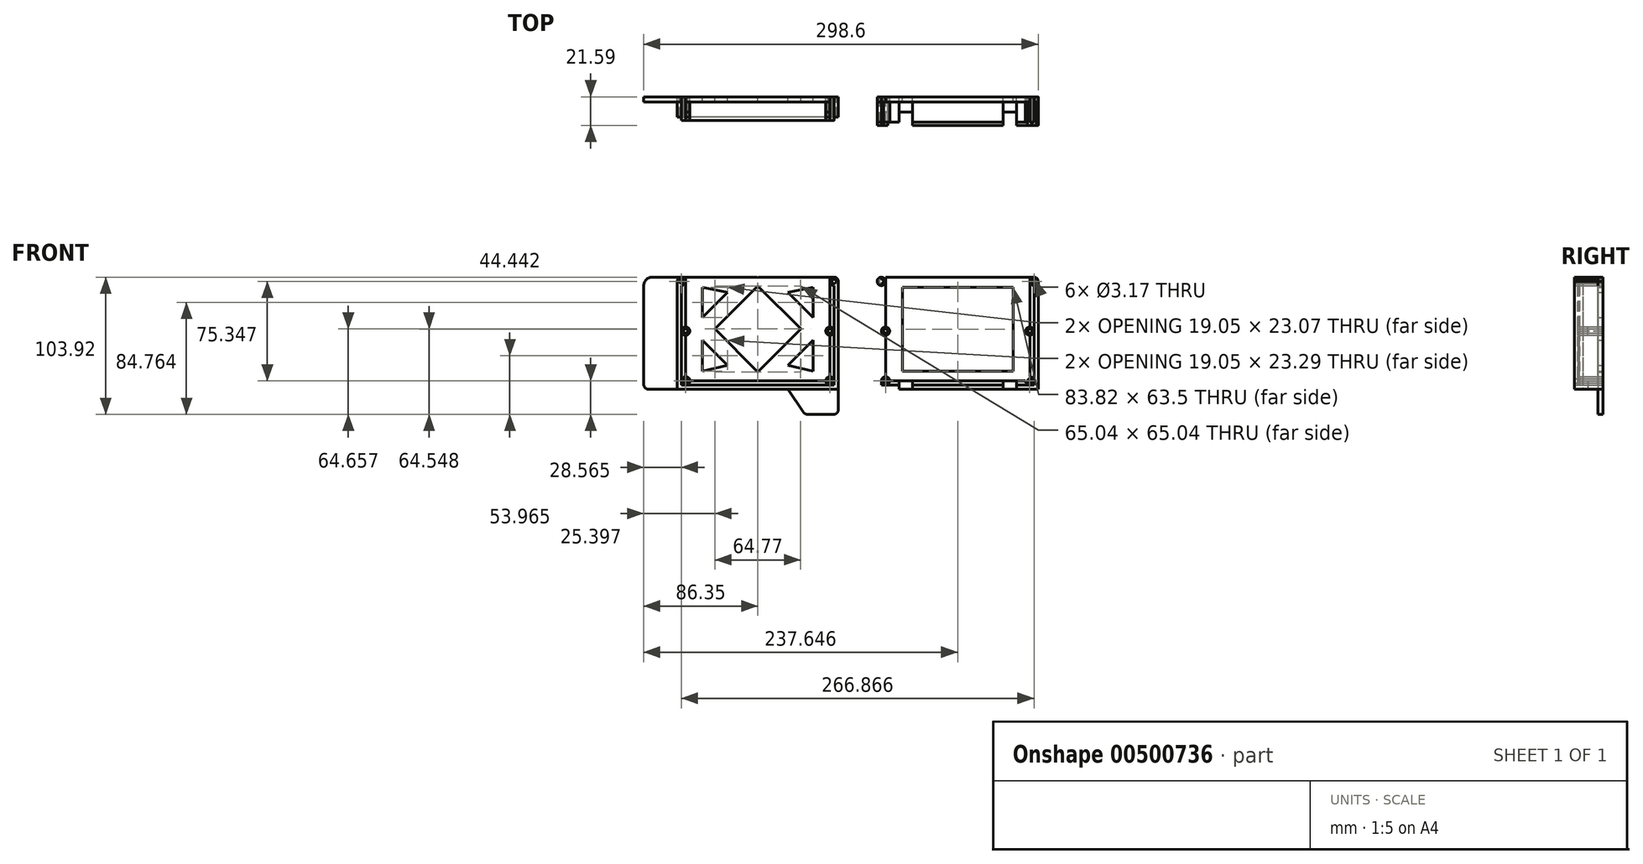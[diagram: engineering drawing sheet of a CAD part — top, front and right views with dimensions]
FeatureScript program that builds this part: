
annotation { "Feature Type Name" : "Feature", "Feature Type Description" : "" }
export const myFeature = defineFeature(function(context is Context, id is Id, definition is map)
    precondition{}
    {
        {
            var Q0;
            Q0=qCreatedBy(makeId("Front.planeOp"),FACE);
            var sketch = newSketch(context, id + "F0", { "sketchPlane" : qUnion([Q0])});
            skLineSegment(sketch, "E0.bottom", {"start": v(57.79, -40.85) * mm, "end": v(-57.78, -40.85) * mm});
            skLineSegment(sketch, "E0.top", {"start": v(57.79, 40.85) * mm, "end": v(-57.79, 40.85) * mm});
            skPoint(sketch, "E0.middle", {"position": v(0, 0) * mm});
            skLineSegment(sketch, "E1.0", {"start": v(51.44, -37.67) * mm, "end": v(-51.34, -37.67) * mm});
            skLineSegment(sketch, "E2.0", {"start": v(-54.61, -34.5) * mm, "end": v(-54.61, -3.17) * mm});
            skLineSegment(sketch, "E3.0", {"start": v(54.6, -34.5) * mm, "end": v(54.6, -3.17) * mm});
            skLineSegment(sketch, "E4.0", {"start": v(-41.91, -30.27) * mm, "end": v(-41.91, -6.98) * mm});
            skLineSegment(sketch, "E5.0", {"start": v(41.91, -30.27) * mm, "end": v(41.91, -6.98) * mm});
            skLineSegment(sketch, "E6", {"start": v(-41.91, 10.16) * mm, "end": v(-22.86, 29.21) * mm});
            skLineSegment(sketch, "E7", {"start": v(-41.91, -6.98) * mm, "end": v(-22.86, -26.03) * mm});
            skLineSegment(sketch, "E8", {"start": v(22.86, -26.03) * mm, "end": v(41.9, -6.98) * mm});
            skLineSegment(sketch, "E9", {"start": v(41.9, 10.16) * mm, "end": v(22.86, 29.21) * mm});
            skLineSegment(sketch, "E10.trimOffspring", {"start": v(-41.91, 10.16) * mm, "end": v(-41.91, 33.23) * mm});
            skLineSegment(sketch, "E11.trimOffspring", {"start": v(41.91, 10.16) * mm, "end": v(41.91, 33.23) * mm});
            skLineSegment(sketch, "E12.trimOffspring", {"start": v(-22.86, 29.21) * mm, "end": v(-41.91, 33.23) * mm});
            skLineSegment(sketch, "E13.trimOffspring", {"start": v(-22.86, -26.03) * mm, "end": v(-41.91, -30.27) * mm});
            skLineSegment(sketch, "E14.trimOffspring", {"start": v(41.91, 33.23) * mm, "end": v(22.86, 29.21) * mm});
            skLineSegment(sketch, "E15.trimOffspring", {"start": v(41.91, -30.27) * mm, "end": v(22.86, -26.03) * mm});
            skLineSegment(sketch, "E16.0", {"start": v(-32.52, 1.59) * mm, "end": v(0, 34.1) * mm});
            skLineSegment(sketch, "E17.0", {"start": v(32.52, 1.59) * mm, "end": v(0, 34.1) * mm});
            skLineSegment(sketch, "E18.0", {"start": v(0, -30.93) * mm, "end": v(32.52, 1.59) * mm});
            skLineSegment(sketch, "E19.0", {"start": v(-32.52, 1.59) * mm, "end": v(0, -30.93) * mm});
            skArc(sketch, "E20", {"start": v(-54.61, -3.17) * mm, "mid": v(-51.44, 0) * mm, "end": v(-54.61, 3.18) * mm});
            skPoint(sketch, "E20.centerSnap0", {"position": v(-57.79, 0) * mm});
            skPoint(sketch, "E21.centerSnap0", {"position": v(57.79, 0) * mm});
            skArc(sketch, "E22", {"start": v(54.6, -34.5) * mm, "mid": v(52.36, -35.43) * mm, "end": v(51.44, -37.67) * mm});
            skPoint(sketch, "E23.second.point", {"position": v(54.6, 38.74) * mm});
            skPoint(sketch, "E23.third.point", {"position": v(60.92, 37.5) * mm});
            skLineSegment(sketch, "E24.trimOffspring", {"start": v(54.6, 3.18) * mm, "end": v(54.6, 40.85) * mm});
            skLineSegment(sketch, "E25.trimOffspring", {"start": v(-54.61, 3.18) * mm, "end": v(-54.61, 40.85) * mm});
            skLineSegment(sketch, "E26", {"start": v(-60.95, 37.67) * mm, "end": v(-60.95, -44.02) * mm});
            skLineSegment(sketch, "E27.0", {"start": v(60.96, -44.02) * mm, "end": v(-60.95, -44.02) * mm});
            skLineSegment(sketch, "E28", {"start": v(-57.79, 40.85) * mm, "end": v(-57.78, -40.85) * mm});
            skLineSegment(sketch, "E29", {"start": v(57.79, 40.85) * mm, "end": v(57.79, -40.85) * mm});
            skLineSegment(sketch, "E30", {"start": v(60.92, 37.5) * mm, "end": v(60.96, -44.02) * mm});
            skPoint(sketch, "E21.center.orphan", {"position": v(54.6, 0) * mm});
            skCircle(sketch, "E31", {"center": v(54.6, 0) * mm, "radius": 3.18 * mm});
            skCircle(sketch, "E32", {"center": v(54.6, 0) * mm, "radius": 1.6 * mm});
            skCircle(sketch, "E33", {"center": v(-54.61, 0) * mm, "radius": 3.18 * mm});
            skCircle(sketch, "E34", {"center": v(-54.61, 0) * mm, "radius": 1.6 * mm});
            skCircle(sketch, "E35", {"center": v(54.6, -37.67) * mm, "radius": 1.59 * mm});
            skCircle(sketch, "E36", {"center": v(54.6, -37.67) * mm, "radius": 3.18 * mm});
            skCircle(sketch, "E37", {"center": v(-54.51, -37.67) * mm, "radius": 3.17 * mm});
            skCircle(sketch, "E38", {"center": v(-54.51, -37.67) * mm, "radius": 1.59 * mm});
            skCircle(sketch, "E39", {"center": v(-57.79, 37.67) * mm, "radius": 3.16 * mm});
            skCircle(sketch, "E40", {"center": v(57.79, 37.67) * mm, "radius": 3.18 * mm});
            skCircle(sketch, "E41", {"center": v(-57.79, 37.67) * mm, "radius": 1.59 * mm});
            skCircle(sketch, "E42", {"center": v(57.79, 37.67) * mm, "radius": 1.6 * mm});
            skLineSegment(sketch, "E43", {"start": v(75.65, 45.82) * mm, "end": v(75.65, -59.82) * mm, "construction": true});
            skCircle(sketch, "E44.MirrorC", {"center": v(93.51, 37.67) * mm, "radius": 1.6 * mm});
            skCircle(sketch, "E45.MirrorC", {"center": v(209.08, 37.67) * mm, "radius": 1.59 * mm});
            skCircle(sketch, "E46.MirrorC", {"center": v(205.8, -37.67) * mm, "radius": 1.59 * mm});
            skCircle(sketch, "E47.MirrorC", {"center": v(96.69, 0) * mm, "radius": 1.6 * mm});
            skCircle(sketch, "E48.MirrorC", {"center": v(205.9, 0) * mm, "radius": 3.18 * mm});
            skCircle(sketch, "E49.MirrorC", {"center": v(96.69, -37.67) * mm, "radius": 1.59 * mm});
            skArc(sketch, "E50.MirrorCS", {"start": v(205.9, -3.17) * mm, "mid": v(202.73, 0) * mm, "end": v(205.9, 3.18) * mm});
            skCircle(sketch, "E51.MirrorC", {"center": v(96.69, 0) * mm, "radius": 3.18 * mm});
            skLineSegment(sketch, "E52.MirrorCS", {"start": v(99.86, -37.67) * mm, "end": v(202.63, -37.67) * mm});
            skLineSegment(sketch, "E53.MirrorCS", {"start": v(209.08, 40.85) * mm, "end": v(209.08, -40.85) * mm});
            skCircle(sketch, "E54.MirrorC", {"center": v(205.9, 0) * mm, "radius": 1.6 * mm});
            skLineSegment(sketch, "E55.MirrorCS", {"start": v(205.9, -34.5) * mm, "end": v(205.9, -3.17) * mm});
            skLineSegment(sketch, "E56.MirrorCS", {"start": v(96.69, -34.5) * mm, "end": v(96.69, -3.17) * mm});
            skPoint(sketch, "E57.MirrorP", {"position": v(209.08, 0) * mm});
            skLineSegment(sketch, "E58.MirrorCS", {"start": v(212.25, 37.67) * mm, "end": v(212.25, -44.02) * mm});
            skArc(sketch, "E59.MirrorCS", {"start": v(96.69, -34.5) * mm, "mid": v(98.93, -35.43) * mm, "end": v(99.86, -37.67) * mm});
            skCircle(sketch, "E60.MirrorC", {"center": v(209.08, 37.67) * mm, "radius": 3.16 * mm});
            skCircle(sketch, "E61.MirrorC", {"center": v(93.51, 37.67) * mm, "radius": 3.18 * mm});
            skLineSegment(sketch, "E62.MirrorCS", {"start": v(96.69, 3.18) * mm, "end": v(96.69, 40.85) * mm});
            skLineSegment(sketch, "E63.MirrorCS", {"start": v(93.51, 40.85) * mm, "end": v(209.08, 40.85) * mm});
            skPoint(sketch, "E64.MirrorP", {"position": v(90.38, 37.5) * mm});
            skLineSegment(sketch, "E65.MirrorCS", {"start": v(93.51, -40.85) * mm, "end": v(209.08, -40.85) * mm});
            skLineSegment(sketch, "E66.MirrorCS", {"start": v(90.38, 37.5) * mm, "end": v(90.34, -44.02) * mm});
            skCircle(sketch, "E67.MirrorC", {"center": v(205.8, -37.67) * mm, "radius": 3.17 * mm});
            skCircle(sketch, "E68.MirrorC", {"center": v(96.69, -37.67) * mm, "radius": 3.18 * mm});
            skLineSegment(sketch, "E69.MirrorCS", {"start": v(90.34, -44.02) * mm, "end": v(212.25, -44.02) * mm});
            skPoint(sketch, "E70.MirrorP", {"position": v(151.3, 0) * mm});
            skPoint(sketch, "E71.MirrorP", {"position": v(93.51, 0) * mm});
            skPoint(sketch, "E72.MirrorP", {"position": v(96.69, 38.74) * mm});
            skLineSegment(sketch, "E73.MirrorCS", {"start": v(205.9, 3.18) * mm, "end": v(205.9, 40.85) * mm});
            skLineSegment(sketch, "E74.MirrorCS", {"start": v(93.51, 40.85) * mm, "end": v(93.51, -40.85) * mm});
            skLineSegment(sketch, "E75", {"start": v(109.39, 33.23) * mm, "end": v(193.2, 33.23) * mm});
            skLineSegment(sketch, "E76", {"start": v(109.39, 33.23) * mm, "end": v(109.39, -30.27) * mm});
            skLineSegment(sketch, "E77", {"start": v(109.39, -30.27) * mm, "end": v(193.2, -30.27) * mm});
            skLineSegment(sketch, "E78", {"start": v(193.2, 33.23) * mm, "end": v(193.2, -30.27) * mm});
            skLineSegment(sketch, "E79.0", {"start": v(185.59, -44.02) * mm, "end": v(185.59, -37.67) * mm});
            skLineSegment(sketch, "E80", {"start": v(195.75, -37.67) * mm, "end": v(195.75, -44.02) * mm});
            skLineSegment(sketch, "E81", {"start": v(117, -37.67) * mm, "end": v(117, -44.02) * mm});
            skLineSegment(sketch, "E82", {"start": v(106.85, -37.67) * mm, "end": v(106.85, -44.02) * mm});
            skLineSegment(sketch, "E83.0", {"start": v(-86.35, 34.5) * mm, "end": v(-86.35, -40.21) * mm});
            skLineSegment(sketch, "E84", {"start": v(-57.79, 40.85) * mm, "end": v(-80, 40.85) * mm});
            skLineSegment(sketch, "E85", {"start": v(-60.95, -44.02) * mm, "end": v(-82.54, -44.02) * mm});
            skPoint(sketch, "E86.visualSharp", {"position": v(-86.35, 40.85) * mm});
            skArc(sketch, "E86.filletArc", {"start": v(-80, 40.85) * mm, "mid": v(-84.49, 38.99) * mm, "end": v(-86.35, 34.5) * mm});
            skPoint(sketch, "E87.visualSharp", {"position": v(-86.35, -44.02) * mm});
            skArc(sketch, "E87.filletArc", {"start": v(-86.35, -40.21) * mm, "mid": v(-85.23, -42.9) * mm, "end": v(-82.54, -44.02) * mm});
            skLineSegment(sketch, "E88.0", {"start": v(57.15, -63.07) * mm, "end": v(37.6, -63.07) * mm});
            skLineSegment(sketch, "E89", {"start": v(60.96, -44.02) * mm, "end": v(60.96, -59.26) * mm});
            skLineSegment(sketch, "E90", {"start": v(22.86, -44.02) * mm, "end": v(34.43, -61.38) * mm});
            skPoint(sketch, "E91.visualSharp", {"position": v(60.96, -63.07) * mm});
            skArc(sketch, "E91.filletArc", {"start": v(57.15, -63.07) * mm, "mid": v(59.84, -61.96) * mm, "end": v(60.96, -59.26) * mm});
            skPoint(sketch, "E92.visualSharp", {"position": v(35.56, -63.07) * mm});
            skArc(sketch, "E92.filletArc", {"start": v(34.43, -61.38) * mm, "mid": v(35.8, -62.62) * mm, "end": v(37.6, -63.07) * mm});
            skSolve(sketch);
        }
        {
            var Q0;
            {var subQ18=sQuery(id+"F0.wireOp",EDGE,"E55.MirrorCS");Q0=makeQuery(id+"F0.imprint","IMPRINT",FACE,{"disambiguationData":[TD([[makeQuery(id+"F0.imprint","IMPRINT",EDGE,{"derivedFrom":subQ18}),1.0]])]});}
            var Q1;
            {var subQ0=sQuery(id+"F0.wireOp",EDGE,"E74.MirrorCS");var subQ1=sQuery(id+"F0.wireOp",EDGE,"E44.MirrorC");var subQ2=makeQuery(id+"F0.imprint","INTERSECT",VERTEX,{"disambiguationData":[OD(0.0)],"derivedFrom":[subQ1,subQ0]});Q1=makeQuery(id+"F0.imprint","IMPRINT",FACE,{"disambiguationData":[TD([[makeQuery(id+"F0.imprint","IMPRINT",EDGE,{"disambiguationData":[TD([[subQ2,1.0]])],"derivedFrom":subQ1}),-1.0]])]});}
            var Q2;
            {var subQ0=sQuery(id+"F0.wireOp",EDGE,"E74.MirrorCS");var subQ1=sQuery(id+"F0.wireOp",EDGE,"E44.MirrorC");var subQ2=makeQuery(id+"F0.imprint","INTERSECT",VERTEX,{"disambiguationData":[OD(0.0)],"derivedFrom":[subQ1,subQ0]});Q2=makeQuery(id+"F0.imprint","IMPRINT",FACE,{"disambiguationData":[TD([[makeQuery(id+"F0.imprint","IMPRINT",EDGE,{"disambiguationData":[TD([[subQ2,-1.0]])],"derivedFrom":subQ1}),-1.0]])]});}
            var Q3;
            Q3=makeQuery(id+"F0.imprint","IMPRINT",FACE,{"disambiguationData":[TD([[makeQuery(id+"F0.imprint","IMPRINT",EDGE,{"derivedFrom":sQuery(id+"F0.wireOp",EDGE,"E49.MirrorC")}),-1.0]])]});
            var Q4;
            Q4=makeQuery(id+"F0.imprint","IMPRINT",FACE,{"disambiguationData":[TD([[makeQuery(id+"F0.imprint","IMPRINT",EDGE,{"derivedFrom":sQuery(id+"F0.wireOp",EDGE,"E46.MirrorC")}),-1.0]])]});
            var Q5;
            {var subQ0=sQuery(id+"F0.wireOp",EDGE,"E53.MirrorCS");var subQ1=sQuery(id+"F0.wireOp",EDGE,"E45.MirrorC");var subQ2=makeQuery(id+"F0.imprint","INTERSECT",VERTEX,{"disambiguationData":[OD(0.0)],"derivedFrom":[subQ1,subQ0]});Q5=makeQuery(id+"F0.imprint","IMPRINT",FACE,{"disambiguationData":[TD([[makeQuery(id+"F0.imprint","IMPRINT",EDGE,{"disambiguationData":[TD([[subQ2,1.0]])],"derivedFrom":subQ1}),-1.0]])]});}
            var Q6;
            {var subQ0=sQuery(id+"F0.wireOp",EDGE,"E53.MirrorCS");var subQ1=sQuery(id+"F0.wireOp",EDGE,"E45.MirrorC");var subQ2=makeQuery(id+"F0.imprint","INTERSECT",VERTEX,{"disambiguationData":[OD(0.0)],"derivedFrom":[subQ1,subQ0]});Q6=makeQuery(id+"F0.imprint","IMPRINT",FACE,{"disambiguationData":[TD([[makeQuery(id+"F0.imprint","IMPRINT",EDGE,{"disambiguationData":[TD([[subQ2,-1.0]])],"derivedFrom":subQ1}),-1.0]])]});}
            extrude(context, id + "F1", {"entities" : qUnion([Q0, Q1, Q2, Q3, Q4, Q5, Q6]), "depth" : 3.8 * mm});
        }
        {
            var Q0;
            Q0=makeQuery(id+"F0.imprint","IMPRINT",FACE,{"disambiguationData":[TD([[makeQuery(id+"F0.imprint","IMPRINT",EDGE,{"derivedFrom":sQuery(id+"F0.wireOp",EDGE,"E47.MirrorC")}),1.0]])]});
            var Q1;
            {var subQ0=sQuery(id+"F0.wireOp",EDGE,"E81");var subQ1=sQuery(id+"F0.wireOp",EDGE,"E52.MirrorCS");var subQ2=makeQuery(id+"F0.imprint","INTERSECT",VERTEX,{"derivedFrom":[subQ1,subQ0]});Q1=makeQuery(id+"F0.imprint","IMPRINT",FACE,{"disambiguationData":[TD([[makeQuery(id+"F0.imprint","IMPRINT",EDGE,{"disambiguationData":[TD([[subQ2,1.0]])],"derivedFrom":subQ1}),-1.0]])]});}
            var Q2;
            {var subQ0=sQuery(id+"F0.wireOp",EDGE,"E82");var subQ1=sQuery(id+"F0.wireOp",EDGE,"E65.MirrorCS");var subQ2=makeQuery(id+"F0.imprint","INTERSECT",VERTEX,{"derivedFrom":[subQ1,subQ0]});Q2=makeQuery(id+"F0.imprint","IMPRINT",FACE,{"disambiguationData":[TD([[makeQuery(id+"F0.imprint","IMPRINT",EDGE,{"disambiguationData":[TD([[subQ2,-1.0]])],"derivedFrom":subQ1}),-1.0]])]});}
            var Q3;
            {var subQ0=sQuery(id+"F0.wireOp",EDGE,"E79.0");var subQ1=sQuery(id+"F0.wireOp",EDGE,"E52.MirrorCS");var subQ2=makeQuery(id+"F0.imprint","INTERSECT",VERTEX,{"derivedFrom":[subQ1,subQ0]});Q3=makeQuery(id+"F0.imprint","IMPRINT",FACE,{"disambiguationData":[TD([[makeQuery(id+"F0.imprint","IMPRINT",EDGE,{"disambiguationData":[TD([[subQ2,-1.0]])],"derivedFrom":subQ1}),-1.0]])]});}
            var Q4;
            {var subQ0=sQuery(id+"F0.wireOp",EDGE,"E79.0");var subQ1=sQuery(id+"F0.wireOp",EDGE,"E65.MirrorCS");var subQ2=makeQuery(id+"F0.imprint","INTERSECT",VERTEX,{"derivedFrom":[subQ1,subQ0]});Q4=makeQuery(id+"F0.imprint","IMPRINT",FACE,{"disambiguationData":[TD([[makeQuery(id+"F0.imprint","IMPRINT",EDGE,{"disambiguationData":[TD([[subQ2,-1.0]])],"derivedFrom":subQ1}),-1.0]])]});}
            var Q5;
            Q5=makeQuery(id+"F0.imprint","IMPRINT",FACE,{"disambiguationData":[TD([[makeQuery(id+"F0.imprint","IMPRINT",EDGE,{"derivedFrom":sQuery(id+"F0.wireOp",EDGE,"E54.MirrorC")}),1.0]])]});
            extrude(context, id + "F2", {"entities" : qUnion([Q0, Q1, Q2, Q3, Q4, Q5]), "operationType" : NewBodyOperationType.ADD, "depth" : 11.43 * mm});
        }
        {
            var Q0;
            {var subQ0=sQuery(id+"F0.wireOp",EDGE,"E63.MirrorCS");var subQ1=sQuery(id+"F0.wireOp",EDGE,"E61.MirrorC");var subQ2=makeQuery(id+"F0.imprint","INTERSECT",VERTEX,{"derivedFrom":[subQ1,subQ0]});Q0=makeQuery(id+"F0.imprint","IMPRINT",FACE,{"disambiguationData":[TD([[makeQuery(id+"F0.imprint","IMPRINT",EDGE,{"disambiguationData":[TD([[subQ2,-1.0]])],"derivedFrom":subQ1}),1.0]])]});}
            var Q1;
            {var subQ0=sQuery(id+"F0.wireOp",EDGE,"E62.MirrorCS");var subQ1=sQuery(id+"F0.wireOp",EDGE,"E51.MirrorC");var subQ2=makeQuery(id+"F0.imprint","INTERSECT",VERTEX,{"derivedFrom":[subQ1,subQ0]});Q1=makeQuery(id+"F0.imprint","IMPRINT",FACE,{"disambiguationData":[TD([[makeQuery(id+"F0.imprint","IMPRINT",EDGE,{"disambiguationData":[TD([[subQ2,1.0]])],"derivedFrom":subQ1}),1.0]])]});}
            var Q2;
            {var subQ0=sQuery(id+"F0.wireOp",EDGE,"E56.MirrorCS");var subQ1=sQuery(id+"F0.wireOp",EDGE,"E51.MirrorC");var subQ2=makeQuery(id+"F0.imprint","INTERSECT",VERTEX,{"derivedFrom":[subQ1,subQ0]});Q2=makeQuery(id+"F0.imprint","IMPRINT",FACE,{"disambiguationData":[TD([[makeQuery(id+"F0.imprint","IMPRINT",EDGE,{"disambiguationData":[TD([[subQ2,-1.0]])],"derivedFrom":subQ1}),1.0]])]});}
            var Q3;
            {var subQ0=sQuery(id+"F0.wireOp",EDGE,"E82");var subQ1=sQuery(id+"F0.wireOp",EDGE,"E52.MirrorCS");var subQ2=makeQuery(id+"F0.imprint","INTERSECT",VERTEX,{"derivedFrom":[subQ1,subQ0]});Q3=makeQuery(id+"F0.imprint","IMPRINT",FACE,{"disambiguationData":[TD([[makeQuery(id+"F0.imprint","IMPRINT",EDGE,{"disambiguationData":[TD([[subQ2,1.0]])],"derivedFrom":subQ1}),-1.0]])]});}
            var Q4;
            {var subQ0=sQuery(id+"F0.wireOp",EDGE,"E79.0");var subQ1=sQuery(id+"F0.wireOp",EDGE,"E52.MirrorCS");var subQ2=makeQuery(id+"F0.imprint","INTERSECT",VERTEX,{"derivedFrom":[subQ1,subQ0]});Q4=makeQuery(id+"F0.imprint","IMPRINT",FACE,{"disambiguationData":[TD([[makeQuery(id+"F0.imprint","IMPRINT",EDGE,{"disambiguationData":[TD([[subQ2,1.0]])],"derivedFrom":subQ1}),-1.0]])]});}
            var Q5;
            {var subQ0=sQuery(id+"F0.wireOp",EDGE,"E55.MirrorCS");Q5=makeQuery(id+"F0.imprint","IMPRINT",FACE,{"disambiguationData":[TD([[makeQuery(id+"F0.imprint","IMPRINT",EDGE,{"derivedFrom":subQ0}),-1.0]])]});}
            var Q6;
            {var subQ8=sQuery(id+"F0.wireOp",EDGE,"E73.MirrorCS");Q6=makeQuery(id+"F0.imprint","IMPRINT",FACE,{"disambiguationData":[TD([[makeQuery(id+"F0.imprint","IMPRINT",EDGE,{"derivedFrom":subQ8}),-1.0]])]});}
            var Q7;
            {var subQ0=sQuery(id+"F0.wireOp",EDGE,"E74.MirrorCS");var subQ1=sQuery(id+"F0.wireOp",EDGE,"E65.MirrorCS");var subQ2=makeQuery(id+"F0.imprint","INTERSECT",VERTEX,{"derivedFrom":[subQ1,subQ0]});Q7=makeQuery(id+"F0.imprint","IMPRINT",FACE,{"disambiguationData":[TD([[makeQuery(id+"F0.imprint","IMPRINT",EDGE,{"disambiguationData":[TD([[subQ2,-1.0]])],"derivedFrom":subQ1}),1.0]])]});}
            extrude(context, id + "F3", {"entities" : qUnion([Q0, Q1, Q2, Q3, Q4, Q5, Q6, Q7]), "depth" : 19.05 * mm});
        }
        {
            var Q0;
            {var subQ6=sQuery(id+"F0.wireOp",EDGE,"E61.MirrorC");var subQ12=sQuery(id+"F0.wireOp",EDGE,"E66.MirrorCS");var subQ17=makeQuery(id+"F0.imprint","INTERSECT",VERTEX,{"derivedFrom":[subQ6,subQ12]});Q0=makeQuery(id+"F0.imprint","IMPRINT",FACE,{"disambiguationData":[TD([[makeQuery(id+"F0.imprint","IMPRINT",EDGE,{"disambiguationData":[TD([[subQ17,1.0]])],"derivedFrom":subQ6}),1.0]])]});}
            var Q1;
            {var subQ0=sQuery(id+"F0.wireOp",EDGE,"E81");var subQ1=sQuery(id+"F0.wireOp",EDGE,"E65.MirrorCS");var subQ2=makeQuery(id+"F0.imprint","INTERSECT",VERTEX,{"derivedFrom":[subQ1,subQ0]});Q1=makeQuery(id+"F0.imprint","IMPRINT",FACE,{"disambiguationData":[TD([[makeQuery(id+"F0.imprint","IMPRINT",EDGE,{"disambiguationData":[TD([[subQ2,-1.0]])],"derivedFrom":subQ1}),-1.0]])]});}
            var Q2;
            {var subQ1=sQuery(id+"F0.wireOp",EDGE,"E58.MirrorCS");Q2=makeQuery(id+"F0.imprint","IMPRINT",FACE,{"disambiguationData":[TD([[makeQuery(id+"F0.imprint","IMPRINT",EDGE,{"derivedFrom":subQ1}),-1.0]])]});}
            var Q3;
            Q3=makeQuery(id+"F0.imprint","IMPRINT",FACE,{"disambiguationData":[TD([[makeQuery(id+"F0.imprint","IMPRINT",EDGE,{"derivedFrom":sQuery(id+"F0.wireOp",EDGE,"E46.MirrorC")}),1.0]])]});
            var Q4;
            Q4=makeQuery(id+"F0.imprint","IMPRINT",FACE,{"disambiguationData":[TD([[makeQuery(id+"F0.imprint","IMPRINT",EDGE,{"derivedFrom":sQuery(id+"F0.wireOp",EDGE,"E49.MirrorC")}),1.0]])]});
            var Q5;
            {var subQ4=sQuery(id+"F0.wireOp",EDGE,"E74.MirrorCS");var subQ7=sQuery(id+"F0.wireOp",EDGE,"E44.MirrorC");var subQ9=makeQuery(id+"F0.imprint","INTERSECT",VERTEX,{"disambiguationData":[OD(0.0)],"derivedFrom":[subQ7,subQ4]});Q5=makeQuery(id+"F0.imprint","IMPRINT",FACE,{"disambiguationData":[TD([[makeQuery(id+"F0.imprint","IMPRINT",EDGE,{"disambiguationData":[TD([[subQ9,1.0]])],"derivedFrom":subQ7}),1.0]])]});}
            var Q6;
            {var subQ2=sQuery(id+"F0.wireOp",EDGE,"E53.MirrorCS");var subQ4=sQuery(id+"F0.wireOp",EDGE,"E45.MirrorC");var subQ5=makeQuery(id+"F0.imprint","INTERSECT",VERTEX,{"disambiguationData":[OD(0.0)],"derivedFrom":[subQ4,subQ2]});Q6=makeQuery(id+"F0.imprint","IMPRINT",FACE,{"disambiguationData":[TD([[makeQuery(id+"F0.imprint","IMPRINT",EDGE,{"disambiguationData":[TD([[subQ5,-1.0]])],"derivedFrom":subQ4}),1.0]])]});}
            var Q7;
            {var subQ3=sQuery(id+"F0.wireOp",EDGE,"E74.MirrorCS");var subQ8=sQuery(id+"F0.wireOp",EDGE,"E44.MirrorC");var subQ9=makeQuery(id+"F0.imprint","INTERSECT",VERTEX,{"disambiguationData":[OD(0.0)],"derivedFrom":[subQ8,subQ3]});Q7=makeQuery(id+"F0.imprint","IMPRINT",FACE,{"disambiguationData":[TD([[makeQuery(id+"F0.imprint","IMPRINT",EDGE,{"disambiguationData":[TD([[subQ9,-1.0]])],"derivedFrom":subQ8}),1.0]])]});}
            var Q8;
            {var subQ0=sQuery(id+"F0.wireOp",EDGE,"E53.MirrorCS");var subQ1=sQuery(id+"F0.wireOp",EDGE,"E45.MirrorC");var subQ2=makeQuery(id+"F0.imprint","INTERSECT",VERTEX,{"disambiguationData":[OD(0.0)],"derivedFrom":[subQ1,subQ0]});Q8=makeQuery(id+"F0.imprint","IMPRINT",FACE,{"disambiguationData":[TD([[makeQuery(id+"F0.imprint","IMPRINT",EDGE,{"disambiguationData":[TD([[subQ2,1.0]])],"derivedFrom":subQ1}),1.0]])]});}
            extrude(context, id + "F4", {"entities" : qUnion([Q0, Q1, Q2, Q3, Q4, Q5, Q6, Q7, Q8]), "depth" : 21.59 * mm});
        }
        {
            var Q0;
            {var subQ10=sQuery(id+"F0.wireOp",EDGE,"E2.0");Q0=makeQuery(id+"F0.imprint","IMPRINT",FACE,{"disambiguationData":[TD([[makeQuery(id+"F0.imprint","IMPRINT",EDGE,{"derivedFrom":subQ10}),-1.0]])]});}
            var Q1;
            {var subQ1=sQuery(id+"F0.wireOp",EDGE,"E26");Q1=makeQuery(id+"F0.imprint","IMPRINT",FACE,{"disambiguationData":[TD([[makeQuery(id+"F0.imprint","IMPRINT",EDGE,{"derivedFrom":subQ1}),-1.0]])]});}
            var Q2;
            Q2=makeQuery(id+"F0.imprint","IMPRINT",FACE,{"disambiguationData":[TD([[makeQuery(id+"F0.imprint","IMPRINT",EDGE,{"derivedFrom":sQuery(id+"F0.wireOp",EDGE,"E88.0")}),-1.0]])]});
            extrude(context, id + "F5", {"entities" : qUnion([Q0, Q1, Q2]), "depth" : 3.8 * mm});
        }
        {
            var Q0;
            Q0=makeQuery(id+"F0.imprint","IMPRINT",FACE,{"disambiguationData":[TD([[makeQuery(id+"F0.imprint","IMPRINT",EDGE,{"derivedFrom":sQuery(id+"F0.wireOp",EDGE,"E34")}),-1.0]])]});
            var Q1;
            Q1=makeQuery(id+"F0.imprint","IMPRINT",FACE,{"disambiguationData":[TD([[makeQuery(id+"F0.imprint","IMPRINT",EDGE,{"derivedFrom":sQuery(id+"F0.wireOp",EDGE,"E32")}),-1.0]])]});
            extrude(context, id + "F6", {"entities" : qUnion([Q0, Q1]), "depth" : 11.43 * mm});
        }
        {
            var Q0;
            {var subQ7=sQuery(id+"F0.wireOp",EDGE,"E25.trimOffspring");Q0=makeQuery(id+"F0.imprint","IMPRINT",FACE,{"disambiguationData":[TD([[makeQuery(id+"F0.imprint","IMPRINT",EDGE,{"derivedFrom":subQ7}),1.0]])]});}
            var Q1;
            {var subQ5=sQuery(id+"F0.wireOp",EDGE,"E2.0");Q1=makeQuery(id+"F0.imprint","IMPRINT",FACE,{"disambiguationData":[TD([[makeQuery(id+"F0.imprint","IMPRINT",EDGE,{"derivedFrom":subQ5}),1.0]])]});}
            var Q2;
            {var subQ0=sQuery(id+"F0.wireOp",EDGE,"E31");var subQ1=sQuery(id+"F0.wireOp",EDGE,"E3.0");var subQ2=makeQuery(id+"F0.imprint","INTERSECT",VERTEX,{"derivedFrom":[subQ1,subQ0]});Q2=makeQuery(id+"F0.imprint","IMPRINT",FACE,{"disambiguationData":[TD([[makeQuery(id+"F0.imprint","IMPRINT",EDGE,{"disambiguationData":[TD([[subQ2,1.0]])],"derivedFrom":subQ1}),-1.0]])]});}
            var Q3;
            {var subQ0=sQuery(id+"F0.wireOp",EDGE,"E31");var subQ1=sQuery(id+"F0.wireOp",EDGE,"E24.trimOffspring");var subQ2=makeQuery(id+"F0.imprint","INTERSECT",VERTEX,{"derivedFrom":[subQ1,subQ0]});Q3=makeQuery(id+"F0.imprint","IMPRINT",FACE,{"disambiguationData":[TD([[makeQuery(id+"F0.imprint","IMPRINT",EDGE,{"disambiguationData":[TD([[subQ2,-1.0]])],"derivedFrom":subQ1}),-1.0]])]});}
            var Q4;
            {var subQ0=sQuery(id+"F0.wireOp",EDGE,"E24.trimOffspring");var subQ1=sQuery(id+"F0.wireOp",EDGE,"E0.top");var subQ2=makeQuery(id+"F0.imprint","INTERSECT",VERTEX,{"derivedFrom":[subQ1,subQ0]});Q4=makeQuery(id+"F0.imprint","IMPRINT",FACE,{"disambiguationData":[TD([[makeQuery(id+"F0.imprint","IMPRINT",EDGE,{"disambiguationData":[TD([[subQ2,1.0]])],"derivedFrom":subQ1}),1.0]])]});}
            var Q5;
            {var subQ0=sQuery(id+"F0.wireOp",EDGE,"E29");var subQ1=sQuery(id+"F0.wireOp",EDGE,"E0.bottom");var subQ2=makeQuery(id+"F0.imprint","INTERSECT",VERTEX,{"derivedFrom":[subQ1,subQ0]});Q5=makeQuery(id+"F0.imprint","IMPRINT",FACE,{"disambiguationData":[TD([[makeQuery(id+"F0.imprint","IMPRINT",EDGE,{"disambiguationData":[TD([[subQ2,-1.0]])],"derivedFrom":subQ1}),-1.0]])]});}
            extrude(context, id + "F7", {"entities" : qUnion([Q0, Q1, Q2, Q3, Q4, Q5]), "depth" : 17.78 * mm});
        }
        {
            var Q0;
            {var subQ0=sQuery(id+"F0.wireOp",EDGE,"E39");var subQ2=sQuery(id+"F0.wireOp",EDGE,"E28");var subQ3=makeQuery(id+"F0.imprint","INTERSECT",VERTEX,{"disambiguationData":[OD(0.0)],"derivedFrom":[subQ2,subQ0]});Q0=makeQuery(id+"F0.imprint","IMPRINT",FACE,{"disambiguationData":[TD([[makeQuery(id+"F0.imprint","IMPRINT",EDGE,{"disambiguationData":[TD([[subQ3,-1.0]])],"derivedFrom":subQ2}),-1.0]])]});}
            var Q1;
            {var subQ0=sQuery(id+"F0.wireOp",EDGE,"E39");var subQ1=sQuery(id+"F0.wireOp",EDGE,"E28");var subQ2=makeQuery(id+"F0.imprint","INTERSECT",VERTEX,{"disambiguationData":[OD(0.0)],"derivedFrom":[subQ1,subQ0]});Q1=makeQuery(id+"F0.imprint","IMPRINT",FACE,{"disambiguationData":[TD([[makeQuery(id+"F0.imprint","IMPRINT",EDGE,{"disambiguationData":[TD([[subQ2,-1.0]])],"derivedFrom":subQ1}),1.0]])]});}
            var Q2;
            {var subQ19=sQuery(id+"F0.wireOp",EDGE,"E26");Q2=makeQuery(id+"F0.imprint","IMPRINT",FACE,{"disambiguationData":[TD([[makeQuery(id+"F0.imprint","IMPRINT",EDGE,{"derivedFrom":subQ19}),1.0]])]});}
            var Q3;
            {var subQ0=sQuery(id+"F0.wireOp",EDGE,"E29");var subQ1=sQuery(id+"F0.wireOp",EDGE,"E0.top");var subQ2=makeQuery(id+"F0.imprint","INTERSECT",VERTEX,{"derivedFrom":[subQ1,subQ0]});Q3=makeQuery(id+"F0.imprint","IMPRINT",FACE,{"disambiguationData":[TD([[makeQuery(id+"F0.imprint","IMPRINT",EDGE,{"disambiguationData":[TD([[subQ2,-1.0]])],"derivedFrom":subQ1}),-1.0]])]});}
            var Q4;
            {var subQ0=sQuery(id+"F0.wireOp",EDGE,"E29");var subQ1=sQuery(id+"F0.wireOp",EDGE,"E0.top");var subQ2=makeQuery(id+"F0.imprint","INTERSECT",VERTEX,{"derivedFrom":[subQ1,subQ0]});Q4=makeQuery(id+"F0.imprint","IMPRINT",FACE,{"disambiguationData":[TD([[makeQuery(id+"F0.imprint","IMPRINT",EDGE,{"disambiguationData":[TD([[subQ2,-1.0]])],"derivedFrom":subQ1}),1.0]])]});}
            var Q5;
            {var subQ0=sQuery(id+"F0.wireOp",EDGE,"E22");Q5=makeQuery(id+"F0.imprint","IMPRINT",FACE,{"disambiguationData":[TD([[makeQuery(id+"F0.imprint","IMPRINT",EDGE,{"derivedFrom":subQ0}),1.0]])]});}
            var Q6;
            Q6=makeQuery(id+"F0.imprint","IMPRINT",FACE,{"disambiguationData":[TD([[makeQuery(id+"F0.imprint","IMPRINT",EDGE,{"derivedFrom":sQuery(id+"F0.wireOp",EDGE,"E38")}),-1.0]])]});
            extrude(context, id + "F8", {"entities" : qUnion([Q0, Q1, Q2, Q3, Q4, Q5, Q6]), "depth" : 15.24 * mm});
        }
    });
